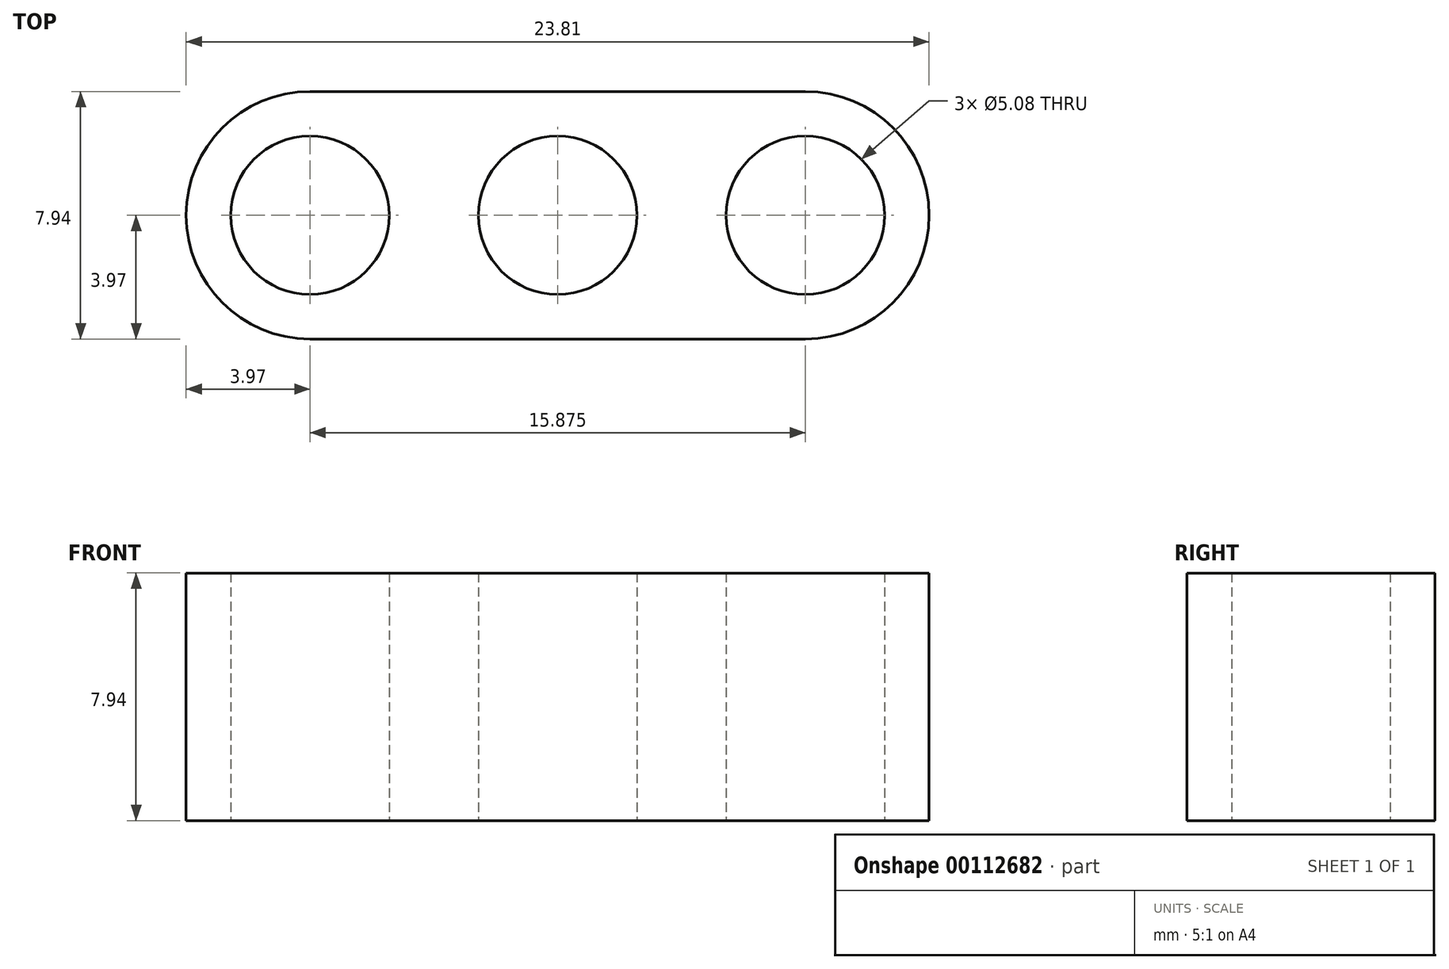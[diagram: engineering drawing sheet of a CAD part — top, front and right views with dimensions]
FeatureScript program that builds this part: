
annotation { "Feature Type Name" : "Feature", "Feature Type Description" : "" }
export const myFeature = defineFeature(function(context is Context, id is Id, definition is map)
    precondition{}
    {
        {
            var Q0;
            Q0=qCreatedBy(makeId("Top.planeOp"),FACE);
            var sketch = newSketch(context, id + "F0", { "sketchPlane" : qUnion([Q0])});
            skLineSegment(sketch, "E0", {"start": v(0, 0) * mm, "end": v(7.94, 0) * mm, "construction": true});
            skLineSegment(sketch, "E1", {"start": v(7.94, 0) * mm, "end": v(15.88, 0) * mm, "construction": true});
            skLineSegment(sketch, "E2.bottom", {"start": v(0, 3.97) * mm, "end": v(15.88, 3.97) * mm});
            skLineSegment(sketch, "E2.top", {"start": v(0, -3.97) * mm, "end": v(15.88, -3.97) * mm});
            skLineSegment(sketch, "E2.left", {"start": v(0, 3.97) * mm, "end": v(0, -3.97) * mm, "construction": true});
            skLineSegment(sketch, "E2.right", {"start": v(15.88, 3.97) * mm, "end": v(15.88, -3.97) * mm, "construction": true});
            skArc(sketch, "E3", {"start": v(0, 3.97) * mm, "mid": v(-3.97, 0) * mm, "end": v(0, -3.97) * mm});
            skArc(sketch, "E4", {"start": v(15.88, -3.97) * mm, "mid": v(19.84, 0) * mm, "end": v(15.88, 3.97) * mm});
            skCircle(sketch, "E5", {"center": v(0, 0) * mm, "radius": 2.54 * mm});
            skCircle(sketch, "E6", {"center": v(7.94, 0) * mm, "radius": 2.54 * mm});
            skCircle(sketch, "E7", {"center": v(15.88, 0) * mm, "radius": 2.54 * mm});
            skSolve(sketch);
        }
        {
            var Q0;
            Q0=qSketchRegion(id+"F0",true);
            extrude(context, id + "F1", {"entities" : qUnion([Q0]), "depth" : 7.94 * mm});
        }
    });
